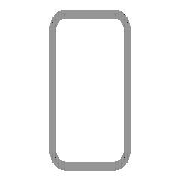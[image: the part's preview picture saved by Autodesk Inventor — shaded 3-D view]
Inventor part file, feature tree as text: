
AUTODESK INVENTOR PART (.ipt)
format: ipt  version: 2025 (Build 290162010, 162A)  size: 132,608 bytes
history: native  units: mm (DEFAULTED — no unit token found)
features: other x4, sketch x1, plane x1
ambient origin geometry x8: Origin, YZ Plane, XZ Plane, XY Plane, X Axis, Y Axis, Z Axis, Center Point
bodies: Solid1 (feature_tree), Body (feature_tree)
feature tree (6):
  parser-record x1  (decoder bookkeeping rows leaked as tree rows — omitted from the tree; the rows remain in map.json)
  other  "Driven Length"
  other  "Start Plane"
  other  "End Plane"
  sketch  "Sketch3"  dims[d3=2200.0mm d4=0.0mm d7=6.0mm d9=40.0mm d11=80.0mm d12=3.0mm d13=-0.0mm d14=2200.0mm d15=20.0mm d16=40.0mm d17=90.0deg d18=2200.0mm]
  plane  "Work Plane3"
